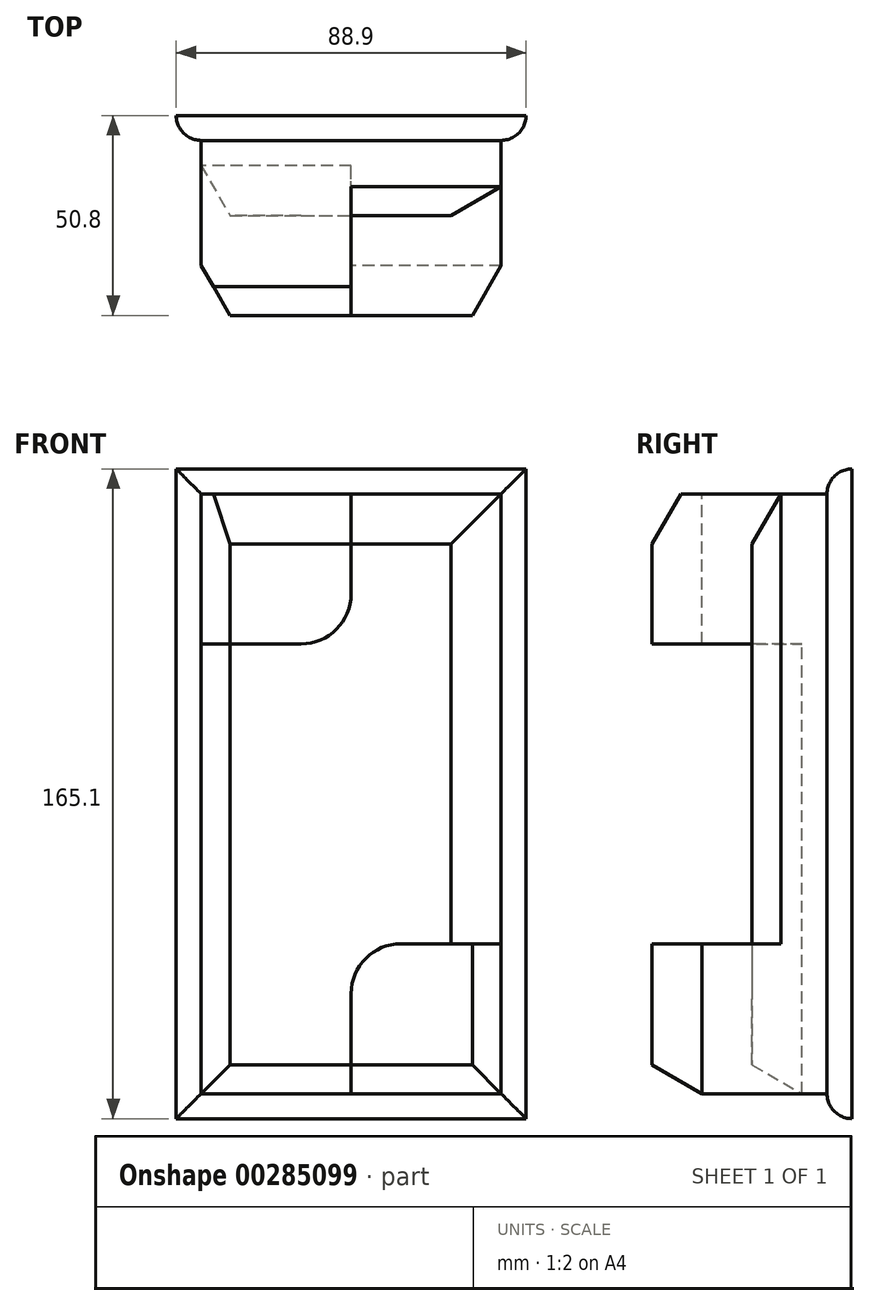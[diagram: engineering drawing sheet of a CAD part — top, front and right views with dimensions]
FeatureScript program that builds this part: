
annotation { "Feature Type Name" : "Feature", "Feature Type Description" : "" }
export const myFeature = defineFeature(function(context is Context, id is Id, definition is map)
    precondition{}
    {
        {
            var Q0;
            Q0=qCreatedBy(makeId("Front.planeOp"),FACE);
            var sketch = newSketch(context, id + "F0", { "sketchPlane" : qUnion([Q0])});
            skLineSegment(sketch, "E0.bottom", {"start": v(-88.9, 0) * mm, "end": v(0, 0) * mm});
            skLineSegment(sketch, "E0.top", {"start": v(-88.9, -165.1) * mm, "end": v(0, -165.1) * mm});
            skLineSegment(sketch, "E0.left", {"start": v(-88.9, 0) * mm, "end": v(-88.9, -165.1) * mm});
            skLineSegment(sketch, "E0.right", {"start": v(0, 0) * mm, "end": v(0, -165.1) * mm});
            skLineSegment(sketch, "E1.0", {"start": v(-82.55, -6.35) * mm, "end": v(-82.55, -158.75) * mm});
            skLineSegment(sketch, "E1.1", {"start": v(-82.55, -6.35) * mm, "end": v(-6.35, -6.35) * mm});
            skLineSegment(sketch, "E1.2", {"start": v(-6.35, -6.35) * mm, "end": v(-6.35, -158.75) * mm});
            skLineSegment(sketch, "E1.3", {"start": v(-82.55, -158.75) * mm, "end": v(-6.35, -158.75) * mm});
            skLineSegment(sketch, "E2", {"start": v(-44.45, -6.35) * mm, "end": v(-44.45, -31.75) * mm});
            skLineSegment(sketch, "E3", {"start": v(-57.15, -44.45) * mm, "end": v(-82.55, -44.45) * mm});
            skLineSegment(sketch, "E4", {"start": v(-44.45, -158.75) * mm, "end": v(-44.45, -133.35) * mm});
            skLineSegment(sketch, "E5", {"start": v(-31.75, -120.65) * mm, "end": v(-6.35, -120.65) * mm});
            skPoint(sketch, "E6.visualSharp", {"position": v(-44.45, -44.45) * mm});
            skArc(sketch, "E6.filletArc", {"start": v(-57.15, -44.45) * mm, "mid": v(-48.17, -40.73) * mm, "end": v(-44.45, -31.75) * mm});
            skPoint(sketch, "E7.visualSharp", {"position": v(-44.45, -120.65) * mm});
            skArc(sketch, "E7.filletArc", {"start": v(-31.75, -120.65) * mm, "mid": v(-40.73, -124.37) * mm, "end": v(-44.45, -133.35) * mm});
            skSolve(sketch);
        }
        {
            var Q0;
            Q0=makeQuery(id+"F0.imprint","IMPRINT",FACE,{"disambiguationData":[TD([[makeQuery(id+"F0.imprint","IMPRINT",EDGE,{"derivedFrom":sQuery(id+"F0.wireOp",EDGE,"E0.bottom")}),-1.0]])]});
            extrude(context, id + "F1", {"entities" : qUnion([Q0]), "depth" : 6.35 * mm});
        }
        {
            var Q0;
            {var subQ4=sQuery(id+"F0.wireOp",EDGE,"E2");Q0=makeQuery(id+"F0.imprint","IMPRINT",FACE,{"disambiguationData":[TD([[makeQuery(id+"F0.imprint","IMPRINT",EDGE,{"derivedFrom":subQ4}),1.0]])]});}
            extrude(context, id + "F2", {"entities" : qUnion([Q0]), "operationType" : NewBodyOperationType.ADD, "depth" : 25.4 * mm});
        }
        {
            var Q0;
            {var subQ1=sQuery(id+"F0.wireOp",EDGE,"E2");Q0=makeQuery(id+"F0.imprint","IMPRINT",FACE,{"disambiguationData":[TD([[makeQuery(id+"F0.imprint","IMPRINT",EDGE,{"derivedFrom":subQ1}),-1.0]])]});}
            var Q1;
            {var subQ4=sQuery(id+"F0.wireOp",EDGE,"E4");Q1=makeQuery(id+"F0.imprint","IMPRINT",FACE,{"disambiguationData":[TD([[makeQuery(id+"F0.imprint","IMPRINT",EDGE,{"derivedFrom":subQ4}),-1.0]])]});}
            extrude(context, id + "F3", {"entities" : qUnion([Q0, Q1]), "operationType" : NewBodyOperationType.ADD, "depth" : 50.8 * mm});
        }
        {
            var Q0;
            Q0=makeQuery(id+"F3.opExtrude","CAP_EDGE",EDGE,{"disambiguationData":[OSD([sQuery(id+"F0.wireOp",EDGE,"E1.3")])],"isStart":false});
            var Q1;
            Q1=makeQuery(id+"F3.opExtrude","CAP_EDGE",EDGE,{"disambiguationData":[OSD([sQuery(id+"F0.wireOp",EDGE,"E1.2")])],"isStart":false});
            var Q2;
            Q2=makeQuery(id+"F3.opExtrude","CAP_EDGE",EDGE,{"disambiguationData":[OSD([sQuery(id+"F0.wireOp",EDGE,"E1.0")])],"isStart":false});
            var Q3;
            Q3=makeQuery(id+"F3.opExtrude","CAP_EDGE",EDGE,{"disambiguationData":[OSD([sQuery(id+"F0.wireOp",EDGE,"E1.1")])],"isStart":false});
            var Q4;
            Q4=makeQuery(id+"F2.opExtrude","CAP_EDGE",EDGE,{"disambiguationData":[OSD([sQuery(id+"F0.wireOp",EDGE,"E1.2")])],"isStart":false});
            var Q5;
            Q5=makeQuery(id+"F2.opExtrude","CAP_EDGE",EDGE,{"disambiguationData":[OSD([sQuery(id+"F0.wireOp",EDGE,"E1.1")])],"isStart":false});
            var Q6;
            Q6=makeQuery(id+"F2.opExtrude","CAP_EDGE",EDGE,{"disambiguationData":[OSD([sQuery(id+"F0.wireOp",EDGE,"E1.0")])],"isStart":false});
            var Q7;
            Q7=makeQuery(id+"F2.opExtrude","CAP_EDGE",EDGE,{"disambiguationData":[OSD([sQuery(id+"F0.wireOp",EDGE,"E1.3")])],"isStart":false});
            chamfer(context, id + "F4", {"entities" : qUnion([Q0, Q1, Q2, Q3, Q4, Q5, Q6, Q7]), "chamferType" : ChamferType.OFFSET_ANGLE, "width" : 12.7 * mm, "oppositeDirection" : true, "angle" : 30 * degree, "tangentPropagation" : true});
        }
        {
            var Q0;
            Q0=makeQuery(id+"F1.opExtrude","CAP_EDGE",EDGE,{"disambiguationData":[OSD([sQuery(id+"F0.wireOp",EDGE,"E0.bottom")])],"isStart":false});
            var Q1;
            Q1=makeQuery(id+"F1.opExtrude","CAP_EDGE",EDGE,{"disambiguationData":[OSD([sQuery(id+"F0.wireOp",EDGE,"E0.left")])],"isStart":false});
            var Q2;
            Q2=makeQuery(id+"F1.opExtrude","CAP_EDGE",EDGE,{"disambiguationData":[OSD([sQuery(id+"F0.wireOp",EDGE,"E0.right")])],"isStart":false});
            var Q3;
            Q3=makeQuery(id+"F1.opExtrude","CAP_EDGE",EDGE,{"disambiguationData":[OSD([sQuery(id+"F0.wireOp",EDGE,"E0.top")])],"isStart":false});
            fillet(context, id + "F5", {"entities" : qUnion([Q0, Q1, Q2, Q3]), "radius" : 6.35 * mm, "tangentPropagation" : true, "allowEdgeOverflow" : false});
        }
    });
